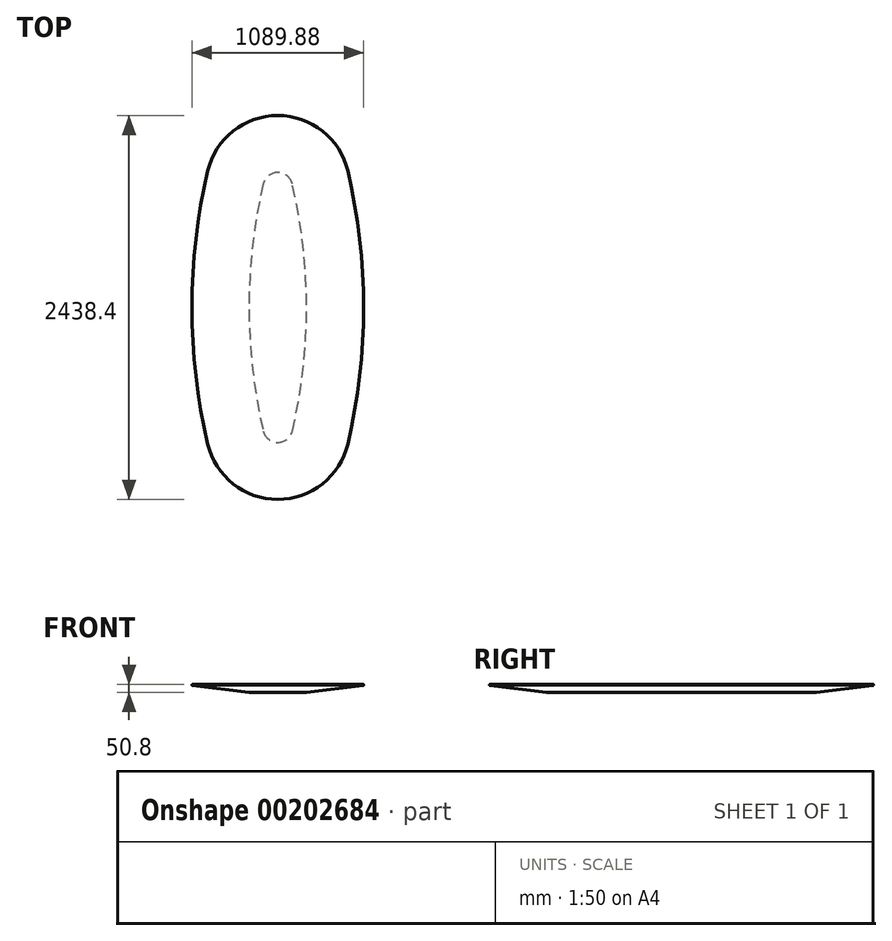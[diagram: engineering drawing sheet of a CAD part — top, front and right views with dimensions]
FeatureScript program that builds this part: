
annotation { "Feature Type Name" : "Feature", "Feature Type Description" : "" }
export const myFeature = defineFeature(function(context is Context, id is Id, definition is map)
    precondition{}
    {
        {
            var Q0;
            Q0=qCreatedBy(makeId("Top.planeOp"),FACE);
            var sketch = newSketch(context, id + "F0", { "sketchPlane" : qUnion([Q0])});
            skCircle(sketch, "E0", {"center": v(0, 762) * mm, "radius": 457.2 * mm});
            skCircle(sketch, "E1", {"center": v(0, -762) * mm, "radius": 457.2 * mm});
            skCircle(sketch, "E2", {"center": v(3265.06, 0) * mm, "radius": 3810 * mm});
            skCircle(sketch, "E3", {"center": v(-3265.06, 0) * mm, "radius": 3810 * mm});
            skSolve(sketch);
        }
        {
            var Q0;
            {var subQ0=sQuery(id+"F0.wireOp",EDGE,"E0");var subQ1=makeQuery(id+"F0.imprint","INTERSECT",VERTEX,{"derivedFrom":[subQ0,sQuery(id+"F0.wireOp",EDGE,"E2")]});Q0=makeQuery(id+"F0.imprint","IMPRINT",FACE,{"disambiguationData":[TD([[makeQuery(id+"F0.imprint","IMPRINT",EDGE,{"disambiguationData":[TD([[subQ1,1.0]])],"derivedFrom":subQ0}),1.0]])]});}
            var Q1;
            {var subQ0=sQuery(id+"F0.wireOp",EDGE,"E1");var subQ1=makeQuery(id+"F0.imprint","INTERSECT",VERTEX,{"derivedFrom":[subQ0,sQuery(id+"F0.wireOp",EDGE,"E2")]});Q1=makeQuery(id+"F0.imprint","IMPRINT",FACE,{"disambiguationData":[TD([[makeQuery(id+"F0.imprint","IMPRINT",EDGE,{"disambiguationData":[TD([[subQ1,-1.0]])],"derivedFrom":subQ0}),1.0]])]});}
            var Q2;
            {var subQ0=sQuery(id+"F0.wireOp",EDGE,"E2");var subQ1=sQuery(id+"F0.wireOp",EDGE,"E0");var subQ2=makeQuery(id+"F0.imprint","INTERSECT",VERTEX,{"derivedFrom":[subQ1,subQ0]});Q2=makeQuery(id+"F0.imprint","IMPRINT",FACE,{"disambiguationData":[TD([[makeQuery(id+"F0.imprint","IMPRINT",EDGE,{"disambiguationData":[TD([[subQ2,-1.0]])],"derivedFrom":subQ1}),-1.0]])]});}
            extrude(context, id + "F1", {"entities" : qUnion([Q0, Q1, Q2]), "depth" : 50.8 * mm});
        }
        {
            var Q0;
            Q0=makeQuery(id+"F1.opExtrude","CAP_FACE",FACE,{"disambiguationData":[OSD([sQuery(id+"F0.wireOp",EDGE,"E0"),sQuery(id+"F0.wireOp",EDGE,"E1"),sQuery(id+"F0.wireOp",EDGE,"E2"),sQuery(id+"F0.wireOp",EDGE,"E3")])],"isStart":true});
            chamfer(context, id + "F2", {"entities" : qUnion([Q0]), "chamferType" : ChamferType.OFFSET_ANGLE, "width" : 44.45 * mm, "oppositeDirection" : false, "angle" : 83 * degree, "tangentPropagation" : true});
        }
        {
            var Q0;
            Q0=makeQuery(id+"F1.opExtrude","CAP_FACE",FACE,{"disambiguationData":[OSD([sQuery(id+"F0.wireOp",EDGE,"E0"),sQuery(id+"F0.wireOp",EDGE,"E1"),sQuery(id+"F0.wireOp",EDGE,"E2"),sQuery(id+"F0.wireOp",EDGE,"E3")])],"isStart":false});
            fillet(context, id + "F3", {"entities" : qUnion([Q0]), "radius" : 3.8 * mm, "tangentPropagation" : true, "allowEdgeOverflow" : false});
        }
        {
            var Q0;
            {var subQ0=sQuery(id+"F0.wireOp",EDGE,"E2");Q0=makeQuery(id+"F2.opChamfer","BLEND_EDGE",EDGE,{"blendedFrom":[makeQuery(id+"F1.opExtrude","CAP_EDGE",EDGE,{"disambiguationData":[OSD([subQ0])],"isStart":true}),makeQuery(id+"F1.opExtrude","SWEPT_FACE",FACE,{"disambiguationData":[OSD([subQ0])]})],"blendedInto":[makeQuery(id+"F1.opExtrude","SWEPT_FACE",FACE,{"disambiguationData":[OSD([subQ0])]})]});}
            var Q1;
            {var subQ0=sQuery(id+"F0.wireOp",EDGE,"E1");Q1=makeQuery(id+"F2.opChamfer","BLEND_EDGE",EDGE,{"blendedFrom":[makeQuery(id+"F1.opExtrude","CAP_EDGE",EDGE,{"disambiguationData":[OSD([subQ0])],"isStart":true}),makeQuery(id+"F1.opExtrude","SWEPT_FACE",FACE,{"disambiguationData":[OSD([subQ0])]})],"blendedInto":[makeQuery(id+"F1.opExtrude","SWEPT_FACE",FACE,{"disambiguationData":[OSD([subQ0])]})]});}
            var Q2;
            {var subQ0=sQuery(id+"F0.wireOp",EDGE,"E3");Q2=makeQuery(id+"F2.opChamfer","BLEND_EDGE",EDGE,{"blendedFrom":[makeQuery(id+"F1.opExtrude","CAP_EDGE",EDGE,{"disambiguationData":[OSD([subQ0])],"isStart":true}),makeQuery(id+"F1.opExtrude","SWEPT_FACE",FACE,{"disambiguationData":[OSD([subQ0])]})],"blendedInto":[makeQuery(id+"F1.opExtrude","SWEPT_FACE",FACE,{"disambiguationData":[OSD([subQ0])]})]});}
            var Q3;
            {var subQ0=sQuery(id+"F0.wireOp",EDGE,"E0");Q3=makeQuery(id+"F2.opChamfer","BLEND_EDGE",EDGE,{"blendedFrom":[makeQuery(id+"F1.opExtrude","CAP_EDGE",EDGE,{"disambiguationData":[OSD([subQ0])],"isStart":true}),makeQuery(id+"F1.opExtrude","SWEPT_FACE",FACE,{"disambiguationData":[OSD([subQ0])]})],"blendedInto":[makeQuery(id+"F1.opExtrude","SWEPT_FACE",FACE,{"disambiguationData":[OSD([subQ0])]})]});}
            fillet(context, id + "F4", {"entities" : qUnion([Q0, Q1, Q2, Q3]), "radius" : 3.8 * mm, "tangentPropagation" : true, "allowEdgeOverflow" : false});
        }
    });
